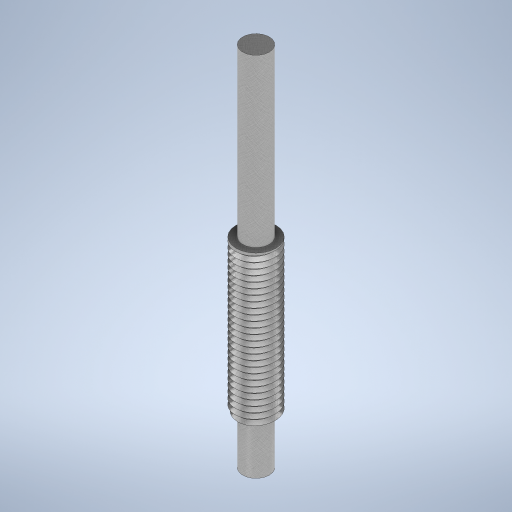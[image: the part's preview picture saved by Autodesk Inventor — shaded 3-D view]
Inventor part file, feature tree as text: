
AUTODESK INVENTOR PART (.ipt)
format: ipt  version: 2024 (Build 280153000, 153)  size: 630,272 bytes
history: native  units: mm
features: sketch x6, extrude x3, helix x1
ambient origin geometry x8: Origin, YZ Plane, XZ Plane, XY Plane, X Axis, Y Axis, Z Axis, Center Point
bodies: Solid1 (feature_tree)
feature tree (10):
  sketch  "Sketch1"  dims[d0=12.0mm d1=45.0mm d2=0.0mm d3=1.7mm]
  extrude  "Extrusion1"  Depth=45.0mm TaperAngle=0.0deg
  helix  "Coil1"  [1 undecoded]
  extrude  "Extrusion2"  Depth=0.2mm
  extrude  "Extrusion3"  Depth=10.0mm
  sketch  "Sketch2"  dims[d4=60.0deg d5=0.2mm]
  sketch  "Sketch3"  dims[d6=0.1mm]
  sketch  "Sketch4"  dims[d7=1.7mm d8=45.0mm d9=10.0mm d10=0.0mm d11=90.0deg d12=90.0deg d13=0.0mm d14=0.0mm d15=8.0mm]
  sketch  "Sketch5"  dims[d16=50.0mm d17=0.0mm]
  sketch  "Sketch6"  dims[d18=8.0mm d19=15.0mm d20=0.0mm]
note: 1 required parameter value undecoded (feature->parameter linkage not recoverable at this tier; creation-order binding heuristic only, values carry confidence <= 0.55)
